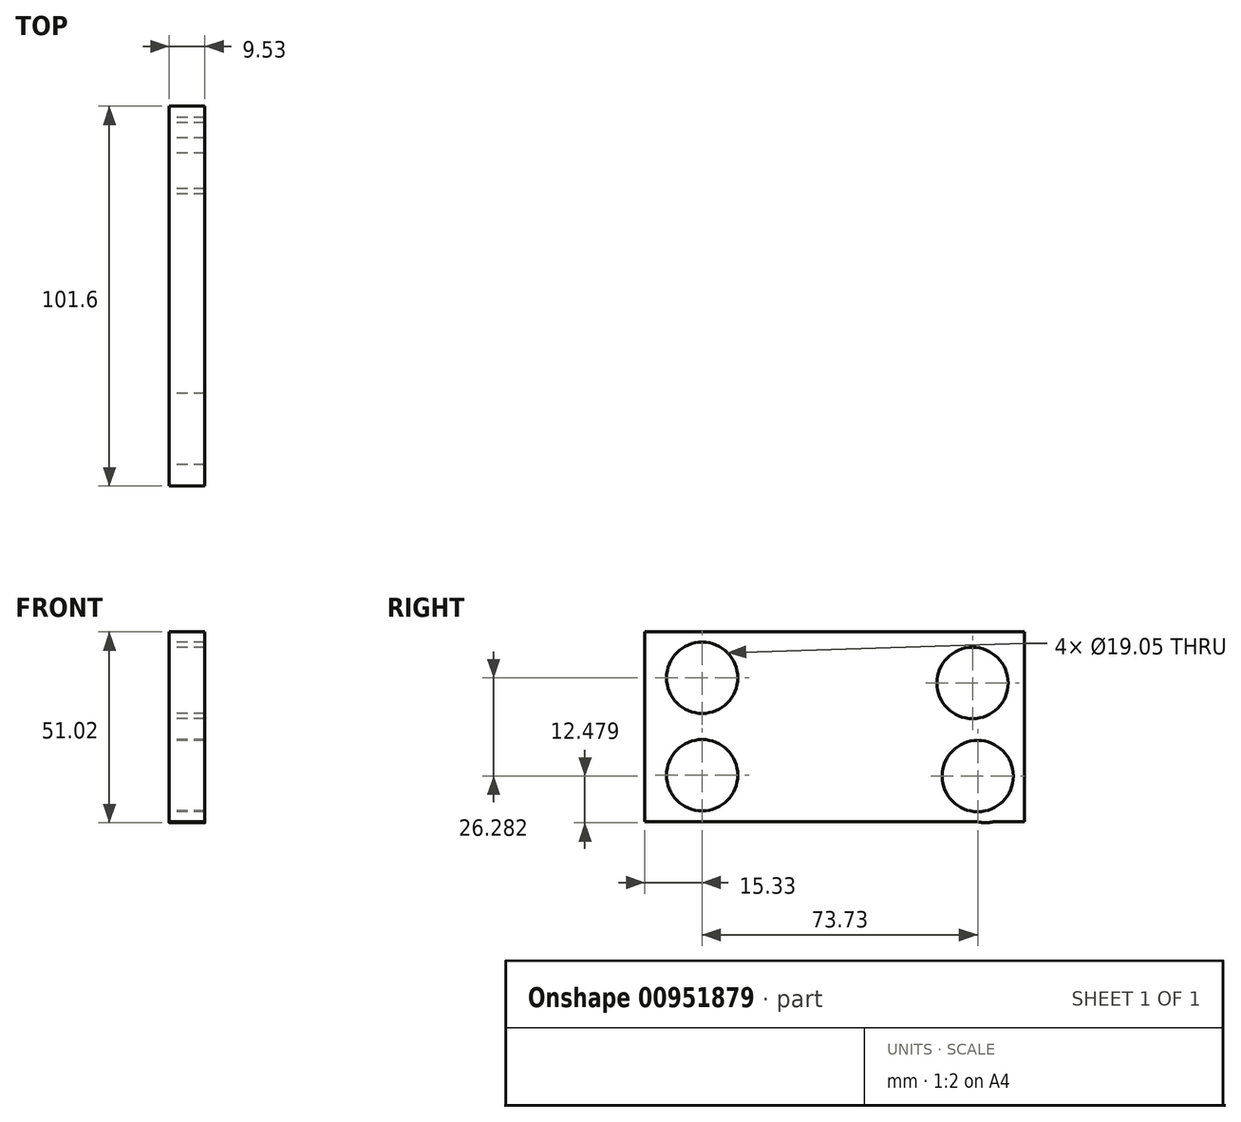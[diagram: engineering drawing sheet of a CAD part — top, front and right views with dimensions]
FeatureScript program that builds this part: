
annotation { "Feature Type Name" : "Feature", "Feature Type Description" : "" }
export const myFeature = defineFeature(function(context is Context, id is Id, definition is map)
    precondition{}
    {
        {
            var Q0;
            Q0=qCreatedBy(makeId("Right.planeOp"),FACE);
            var sketch = newSketch(context, id + "F0", { "sketchPlane" : qUnion([Q0])});
            skLineSegment(sketch, "E0.bottom", {"start": v(-50.8, 25.4) * mm, "end": v(50.8, 25.4) * mm});
            skLineSegment(sketch, "E0.top", {"start": v(-50.8, -25.4) * mm, "end": v(50.8, -25.4) * mm});
            skLineSegment(sketch, "E0.left", {"start": v(-50.8, 25.4) * mm, "end": v(-50.8, -25.4) * mm});
            skLineSegment(sketch, "E0.right", {"start": v(50.8, 25.4) * mm, "end": v(50.8, -25.4) * mm});
            skPoint(sketch, "E0.middle", {"position": v(0, 0) * mm});
            skArc(sketch, "E1", {"start": v(38.32, -25.4) * mm, "mid": v(40.35, -25.62) * mm, "end": v(42.39, -25.4) * mm});
            skCircle(sketch, "E2", {"center": v(36.87, 11.75) * mm, "radius": 9.53 * mm});
            skCircle(sketch, "E3", {"center": v(38.26, -13.14) * mm, "radius": 9.53 * mm});
            skCircle(sketch, "E4", {"center": v(-35.47, 13.14) * mm, "radius": 9.53 * mm});
            skCircle(sketch, "E5", {"center": v(-35.47, -12.9) * mm, "radius": 9.53 * mm});
            skSolve(sketch);
        }
        {
            var Q0;
            Q0 = qSketchRegion(id + "F0", true);
            extrude(context, id + "F1", {"entities" : qUnion([Q0]), "depth" : 9.52 * mm, "offsetDistance" : 25.4 * mm});
        }
    });
